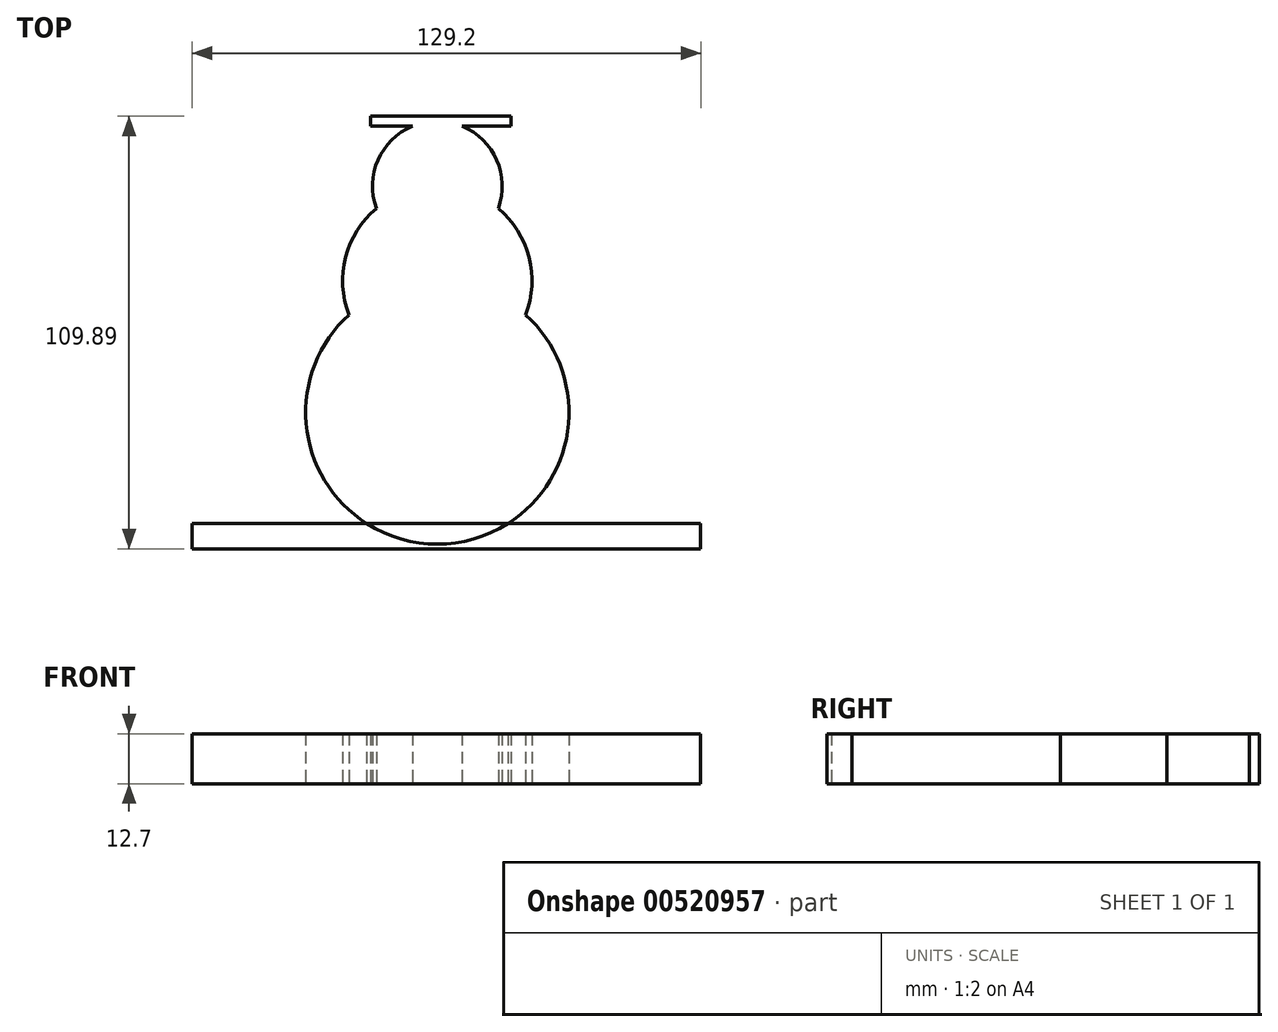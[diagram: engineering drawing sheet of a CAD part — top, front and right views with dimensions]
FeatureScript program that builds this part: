
annotation { "Feature Type Name" : "Feature", "Feature Type Description" : "" }
export const myFeature = defineFeature(function(context is Context, id is Id, definition is map)
    precondition{}
    {
        {
            var Q0;
            Q0=qCreatedBy(makeId("Top.planeOp"),FACE);
            var sketch = newSketch(context, id + "F0", { "sketchPlane" : qUnion([Q0])});
            skCircle(sketch, "E0", {"center": v(0, -41.17) * mm, "radius": 33.45 * mm});
            skCircle(sketch, "E1", {"center": v(0, -7.73) * mm, "radius": 24.05 * mm});
            skCircle(sketch, "E2", {"center": v(0, 16.32) * mm, "radius": 16.49 * mm});
            skLineSegment(sketch, "E3.bottom", {"start": v(0, 31.56) * mm, "end": v(18.69, 31.56) * mm});
            skLineSegment(sketch, "E3.top", {"start": v(0, 34.1) * mm, "end": v(18.69, 34.1) * mm});
            skLineSegment(sketch, "E3.left", {"start": v(0, 31.56) * mm, "end": v(0, 34.1) * mm});
            skLineSegment(sketch, "E3.right", {"start": v(18.69, 31.56) * mm, "end": v(18.69, 34.1) * mm});
            skLineSegment(sketch, "E4.bottom", {"start": v(0, 31.56) * mm, "end": v(-16.94, 31.56) * mm});
            skLineSegment(sketch, "E4.top", {"start": v(0, 34.1) * mm, "end": v(-16.94, 34.1) * mm});
            skLineSegment(sketch, "E4.right", {"start": v(-16.94, 31.56) * mm, "end": v(-16.94, 34.1) * mm});
            skLineSegment(sketch, "E5.bottom", {"start": v(0, 34.1) * mm, "end": v(9.34, 34.1) * mm});
            skLineSegment(sketch, "E5.top", {"start": v(0, 53.15) * mm, "end": v(9.34, 53.15) * mm});
            skLineSegment(sketch, "E5.left", {"start": v(0, 34.1) * mm, "end": v(0, 53.15) * mm});
            skLineSegment(sketch, "E5.right", {"start": v(9.34, 34.1) * mm, "end": v(9.34, 53.15) * mm});
            skPoint(sketch, "E6.oppositeSnap0", {"position": v(-8.47, 34.1) * mm});
            skLineSegment(sketch, "E6.bottom", {"start": v(0, 34.1) * mm, "end": v(-8.47, 34.1) * mm});
            skLineSegment(sketch, "E6.top", {"start": v(0, 53.15) * mm, "end": v(-8.47, 53.15) * mm});
            skLineSegment(sketch, "E6.right", {"start": v(-8.47, 34.1) * mm, "end": v(-8.47, 53.15) * mm});
            skLineSegment(sketch, "E7.bottom", {"start": v(-62.28, -75.79) * mm, "end": v(66.92, -75.79) * mm});
            skLineSegment(sketch, "E7.top", {"start": v(-62.28, -69.41) * mm, "end": v(66.92, -69.41) * mm});
            skLineSegment(sketch, "E7.left", {"start": v(-62.28, -75.79) * mm, "end": v(-62.28, -69.41) * mm});
            skLineSegment(sketch, "E7.right", {"start": v(66.92, -75.79) * mm, "end": v(66.92, -69.41) * mm});
            skSolve(sketch);
        }
        {
            var Q0;
            Q0=makeQuery(id+"F0.imprint","IMPRINT",FACE,{"disambiguationData":[TD([[makeQuery(id+"F0.imprint","IMPRINT",EDGE,{"derivedFrom":sQuery(id+"F0.wireOp",EDGE,"E5.bottom")}),1.0]])]});
            var Q1;
            Q1=makeQuery(id+"F0.imprint","IMPRINT",FACE,{"disambiguationData":[TD([[makeQuery(id+"F0.imprint","IMPRINT",EDGE,{"derivedFrom":sQuery(id+"F0.wireOp",EDGE,"E6.bottom")}),-1.0]])]});
            var Q2;
            Q2=makeQuery(id+"F0.imprint","IMPRINT",FACE,{"disambiguationData":[TD([[makeQuery(id+"F0.imprint","IMPRINT",EDGE,{"derivedFrom":sQuery(id+"F0.wireOp",EDGE,"E4.top")}),1.0]])]});
            var Q3;
            Q3=makeQuery(id+"F0.imprint","IMPRINT",FACE,{"disambiguationData":[TD([[makeQuery(id+"F0.imprint","IMPRINT",EDGE,{"derivedFrom":sQuery(id+"F0.wireOp",EDGE,"E3.top")}),-1.0]])]});
            var Q4;
            {var subQ3=sQuery(id+"F0.wireOp",EDGE,"E2");var subQ5=sQuery(id+"F0.wireOp",EDGE,"E1");var subQ7=makeQuery(id+"F0.imprint","INTERSECT",VERTEX,{"disambiguationData":[OD(0.0)],"derivedFrom":[subQ5,subQ3]});Q4=makeQuery(id+"F0.imprint","IMPRINT",FACE,{"disambiguationData":[TD([[makeQuery(id+"F0.imprint","IMPRINT",EDGE,{"disambiguationData":[TD([[subQ7,1.0]])],"derivedFrom":subQ5}),-1.0]])]});}
            var Q5;
            {var subQ0=sQuery(id+"F0.wireOp",EDGE,"E1");var subQ1=sQuery(id+"F0.wireOp",EDGE,"E0");var subQ2=makeQuery(id+"F0.imprint","INTERSECT",VERTEX,{"disambiguationData":[OD(0.0)],"derivedFrom":[subQ1,subQ0]});Q5=makeQuery(id+"F0.imprint","IMPRINT",FACE,{"disambiguationData":[TD([[makeQuery(id+"F0.imprint","IMPRINT",EDGE,{"disambiguationData":[TD([[subQ2,1.0]])],"derivedFrom":subQ1}),-1.0]])]});}
            var Q6;
            {var subQ0=sQuery(id+"F0.wireOp",EDGE,"E1");var subQ1=sQuery(id+"F0.wireOp",EDGE,"E0");var subQ2=makeQuery(id+"F0.imprint","INTERSECT",VERTEX,{"disambiguationData":[OD(0.0)],"derivedFrom":[subQ1,subQ0]});Q6=makeQuery(id+"F0.imprint","IMPRINT",FACE,{"disambiguationData":[TD([[makeQuery(id+"F0.imprint","IMPRINT",EDGE,{"disambiguationData":[TD([[subQ2,-1.0]])],"derivedFrom":subQ1}),1.0]])]});}
            var Q7;
            {var subQ0=sQuery(id+"F0.wireOp",EDGE,"E1");var subQ1=sQuery(id+"F0.wireOp",EDGE,"E0");var subQ2=makeQuery(id+"F0.imprint","INTERSECT",VERTEX,{"disambiguationData":[OD(0.0)],"derivedFrom":[subQ1,subQ0]});Q7=makeQuery(id+"F0.imprint","IMPRINT",FACE,{"disambiguationData":[TD([[makeQuery(id+"F0.imprint","IMPRINT",EDGE,{"disambiguationData":[TD([[subQ2,1.0]])],"derivedFrom":subQ1}),1.0]])]});}
            var Q8;
            {var subQ0=sQuery(id+"F0.wireOp",EDGE,"E2");var subQ1=sQuery(id+"F0.wireOp",EDGE,"E1");var subQ2=makeQuery(id+"F0.imprint","INTERSECT",VERTEX,{"disambiguationData":[OD(0.0)],"derivedFrom":[subQ1,subQ0]});Q8=makeQuery(id+"F0.imprint","IMPRINT",FACE,{"disambiguationData":[TD([[makeQuery(id+"F0.imprint","IMPRINT",EDGE,{"disambiguationData":[TD([[subQ2,1.0]])],"derivedFrom":subQ1}),1.0]])]});}
            var Q9;
            {var subQ0=sQuery(id+"F0.wireOp",EDGE,"E3.bottom");var subQ1=sQuery(id+"F0.wireOp",EDGE,"E2");var subQ2=makeQuery(id+"F0.imprint","INTERSECT",VERTEX,{"derivedFrom":[subQ1,subQ0]});Q9=makeQuery(id+"F0.imprint","IMPRINT",FACE,{"disambiguationData":[TD([[makeQuery(id+"F0.imprint","IMPRINT",EDGE,{"disambiguationData":[TD([[subQ2,-1.0]])],"derivedFrom":subQ1}),1.0]])]});}
            var Q10;
            {var subQ0=sQuery(id+"F0.wireOp",EDGE,"E4.bottom");var subQ1=sQuery(id+"F0.wireOp",EDGE,"E2");var subQ2=makeQuery(id+"F0.imprint","INTERSECT",VERTEX,{"derivedFrom":[subQ1,subQ0]});Q10=makeQuery(id+"F0.imprint","IMPRINT",FACE,{"disambiguationData":[TD([[makeQuery(id+"F0.imprint","IMPRINT",EDGE,{"disambiguationData":[TD([[subQ2,1.0]])],"derivedFrom":subQ1}),1.0]])]});}
            var Q11;
            Q11=makeQuery(id+"F0.imprint","IMPRINT",FACE,{"disambiguationData":[TD([[makeQuery(id+"F0.imprint","IMPRINT",EDGE,{"derivedFrom":sQuery(id+"F0.wireOp",EDGE,"E7.bottom")}),1.0]])]});
            var Q12;
            {var subQ0=sQuery(id+"F0.wireOp",EDGE,"E7.top");var subQ1=sQuery(id+"F0.wireOp",EDGE,"E0");var subQ2=makeQuery(id+"F0.imprint","INTERSECT",VERTEX,{"disambiguationData":[OD(0.0)],"derivedFrom":[subQ1,subQ0]});Q12=makeQuery(id+"F0.imprint","IMPRINT",FACE,{"disambiguationData":[TD([[makeQuery(id+"F0.imprint","IMPRINT",EDGE,{"disambiguationData":[TD([[subQ2,-1.0]])],"derivedFrom":subQ1}),1.0]])]});}
            extrude(context, id + "F1", {"entities" : qUnion([Q0, Q1, Q2, Q3, Q4, Q5, Q6, Q7, Q8, Q9, Q10, Q11, Q12]), "depth" : 12.7 * mm, "offsetDistance" : 25.4 * mm});
        }
    });
